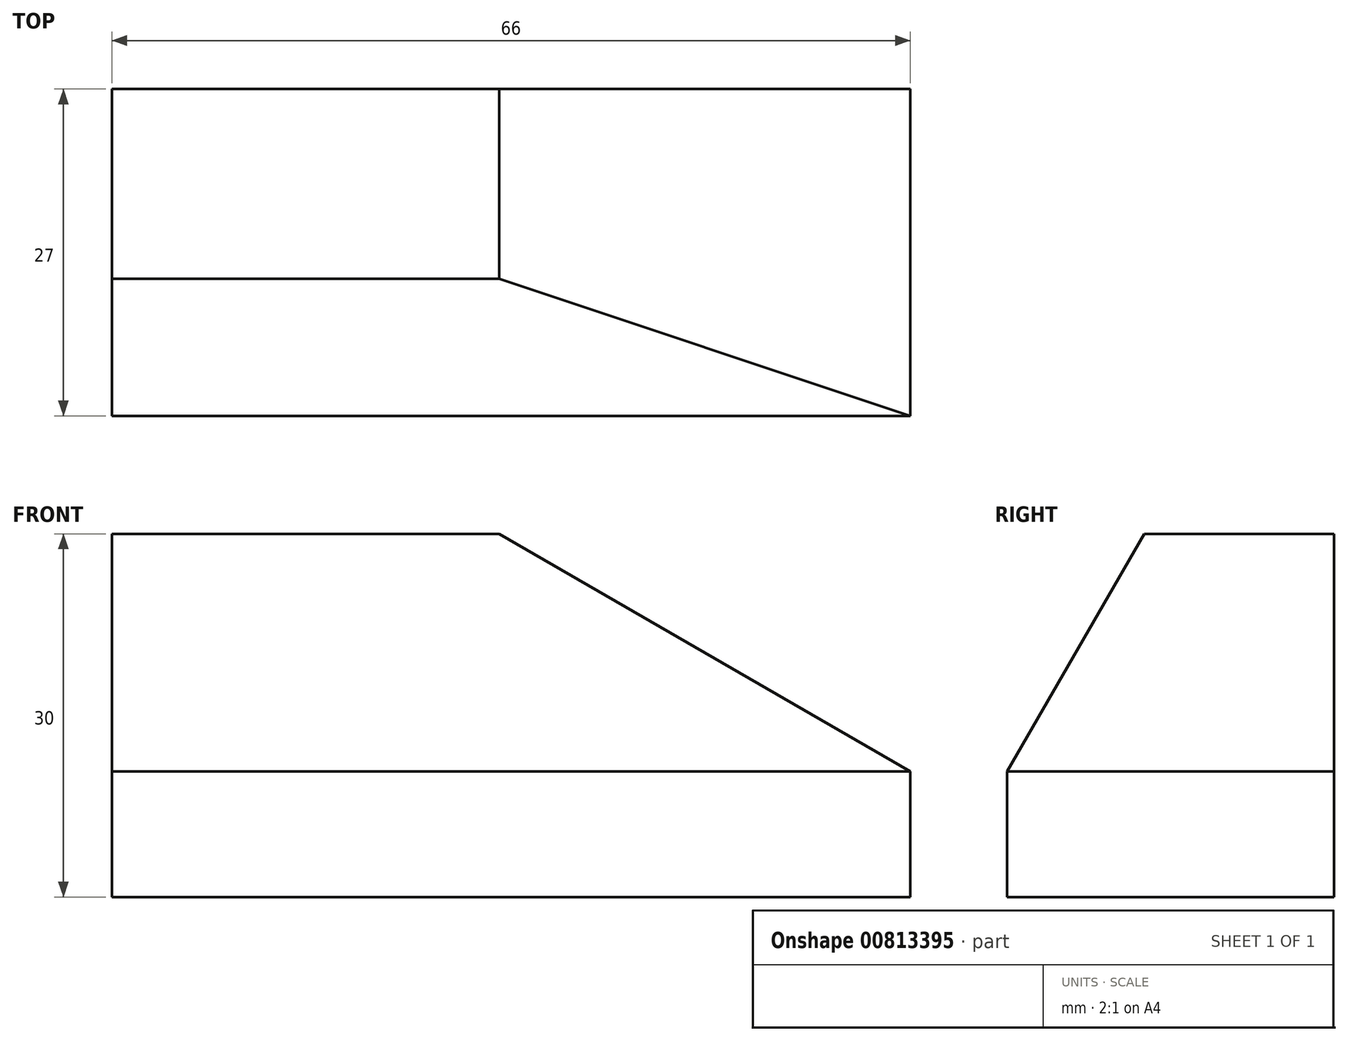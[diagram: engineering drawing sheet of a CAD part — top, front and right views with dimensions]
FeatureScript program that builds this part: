
annotation { "Feature Type Name" : "Feature", "Feature Type Description" : "" }
export const myFeature = defineFeature(function(context is Context, id is Id, definition is map)
    precondition{}
    {
        {
            var Q0;
            Q0=qCreatedBy(makeId("Front.planeOp"),FACE);
            var sketch = newSketch(context, id + "F0", { "sketchPlane" : qUnion([Q0])});
            skLineSegment(sketch, "E0.bottom", {"start": v(0, 0) * mm, "end": v(66, 0) * mm});
            skLineSegment(sketch, "E0.top", {"start": v(0, 30) * mm, "end": v(66, 30) * mm});
            skLineSegment(sketch, "E0.left", {"start": v(0, 0) * mm, "end": v(0, 30) * mm});
            skLineSegment(sketch, "E0.right", {"start": v(66, 0) * mm, "end": v(66, 30) * mm});
            skLineSegment(sketch, "E1", {"start": v(32, 30) * mm, "end": v(66, 10.37) * mm});
            skSolve(sketch);
        }
        {
            var Q0;
            {var subQ1=sQuery(id+"F0.wireOp",EDGE,"E0.bottom");Q0=makeQuery(id+"F0.imprint","IMPRINT",FACE,{"disambiguationData":[TD([[makeQuery(id+"F0.imprint","IMPRINT",EDGE,{"derivedFrom":subQ1}),1.0]])]});}
            extrude(context, id + "F1", {"entities" : qUnion([Q0]), "depth" : 27 * mm, "offsetDistance" : 25 * mm});
        }
        {
            var Q0;
            Q0=makeQuery(id+"F1.opExtrude","SWEPT_FACE",FACE,{"disambiguationData":[OSD([sQuery(id+"F0.wireOp",EDGE,"E0.left")])]});
            var sketch = newSketch(context, id + "F2", { "sketchPlane" : qUnion([Q0])});
            skLineSegment(sketch, "E2.0", {"start": v(27, 10.37) * mm, "end": v(0, 10.37) * mm});
            skLineSegment(sketch, "E3", {"start": v(27, 10.37) * mm, "end": v(15.67, 30) * mm});
            skLineSegment(sketch, "E4.0", {"start": v(27, 30) * mm, "end": v(0, 30) * mm});
            skLineSegment(sketch, "E5.0", {"start": v(27, 0) * mm, "end": v(27, 30) * mm});
            skSolve(sketch);
        }
        {
            var Q0;
            Q0 = qSketchRegion(id + "F2", true);
            extrude(context, id + "F3", {"entities" : qUnion([Q0]), "operationType" : NewBodyOperationType.REMOVE, "endBound" : BoundingType.THROUGH_ALL, "oppositeDirection" : true, "depth" : 25 * mm, "offsetDistance" : 25 * mm});
        }
    });
